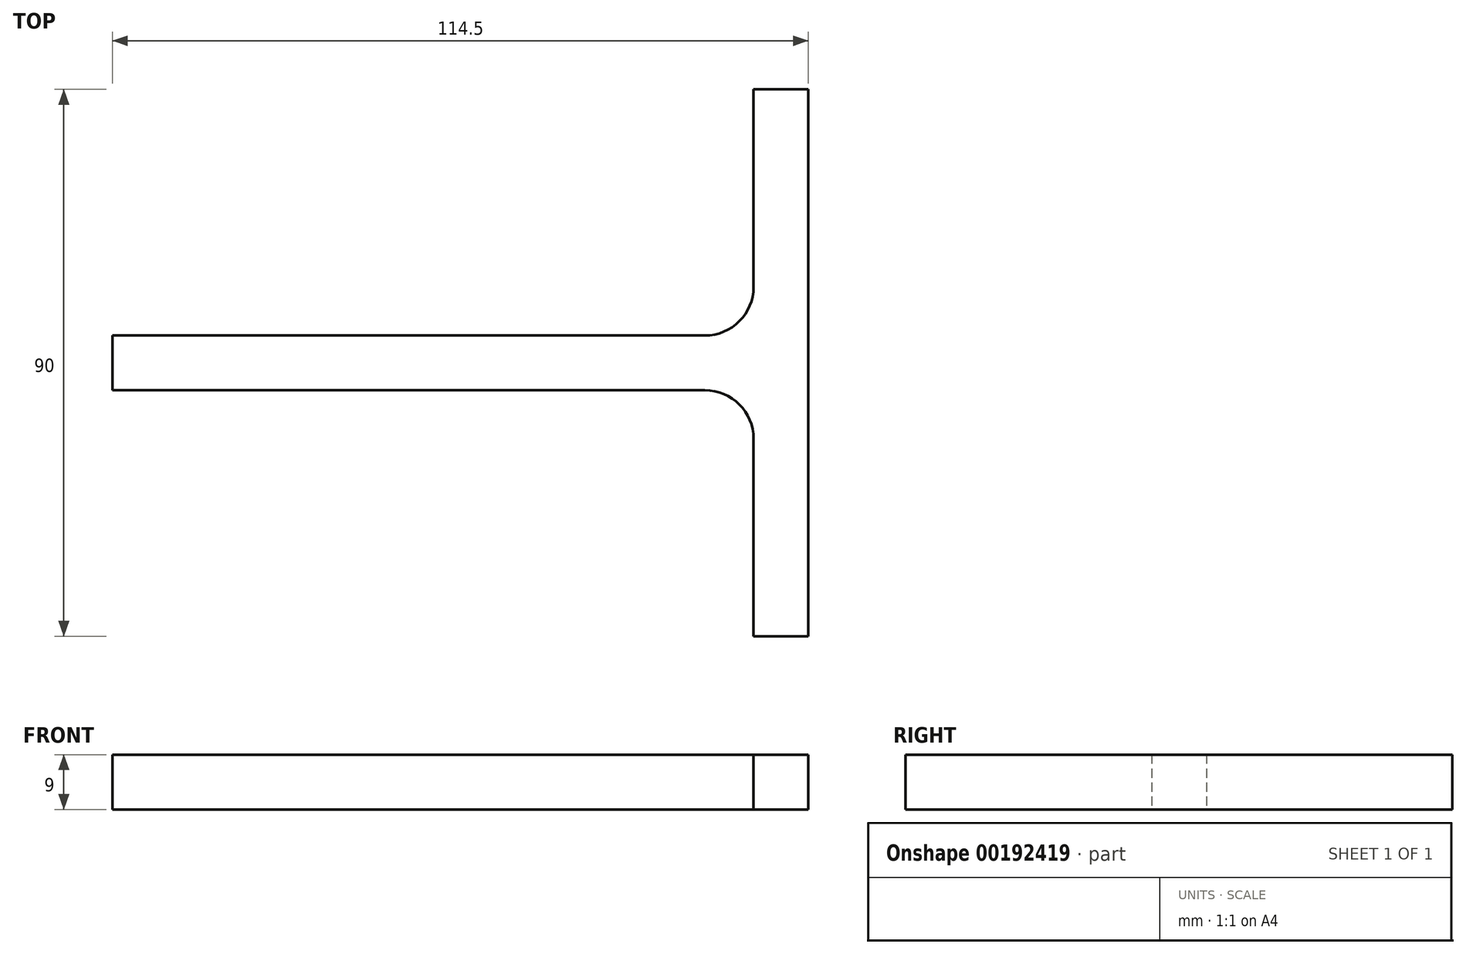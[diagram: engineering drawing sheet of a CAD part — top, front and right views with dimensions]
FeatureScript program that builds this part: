
annotation { "Feature Type Name" : "Feature", "Feature Type Description" : "" }
export const myFeature = defineFeature(function(context is Context, id is Id, definition is map)
    precondition{}
    {
        {
            var Q0;
            Q0=qCreatedBy(makeId("Top.planeOp"),FACE);
            var sketch = newSketch(context, id + "F0", { "sketchPlane" : qUnion([Q0])});
            skLineSegment(sketch, "E0.bottom", {"start": v(-55, -4.5) * mm, "end": v(55, -4.5) * mm});
            skLineSegment(sketch, "E0.top", {"start": v(-55, 4.5) * mm, "end": v(55, 4.5) * mm});
            skLineSegment(sketch, "E0.left", {"start": v(-55, -4.5) * mm, "end": v(-55, 4.5) * mm});
            skLineSegment(sketch, "E0.right", {"start": v(55, -4.5) * mm, "end": v(55, 4.5) * mm});
            skPoint(sketch, "E0.middle", {"position": v(0, 0) * mm});
            skLineSegment(sketch, "E1.bottom", {"start": v(50.5, -45) * mm, "end": v(59.5, -45) * mm});
            skLineSegment(sketch, "E1.top", {"start": v(50.5, 45) * mm, "end": v(59.5, 45) * mm});
            skLineSegment(sketch, "E1.left", {"start": v(50.5, -45) * mm, "end": v(50.5, 45) * mm});
            skLineSegment(sketch, "E1.right", {"start": v(59.5, -45) * mm, "end": v(59.5, 45) * mm});
            skPoint(sketch, "E1.middle", {"position": v(55, 0) * mm});
            skSolve(sketch);
        }
        {
            var Q0;
            Q0 = qSketchRegion(id + "F0", true);
            extrude(context, id + "F1", {"entities" : qUnion([Q0]), "depth" : 9 * mm});
        }
        {
            var Q0;
            Q0=makeQuery(id+"F1.opExtrude","SWEPT_EDGE",EDGE,{"disambiguationData":[OSD([sQuery(id+"F0.wireOp",EDGE,"E0.bottom"),sQuery(id+"F0.wireOp",EDGE,"E1.left")])]});
            var Q1;
            Q1=makeQuery(id+"F1.opExtrude","SWEPT_EDGE",EDGE,{"disambiguationData":[OSD([sQuery(id+"F0.wireOp",EDGE,"E0.top"),sQuery(id+"F0.wireOp",EDGE,"E1.left")])]});
            fillet(context, id + "F2", {"entities" : qUnion([Q0, Q1]), "radius" : 8 * mm, "tangentPropagation" : true, "allowEdgeOverflow" : false});
        }
    });
